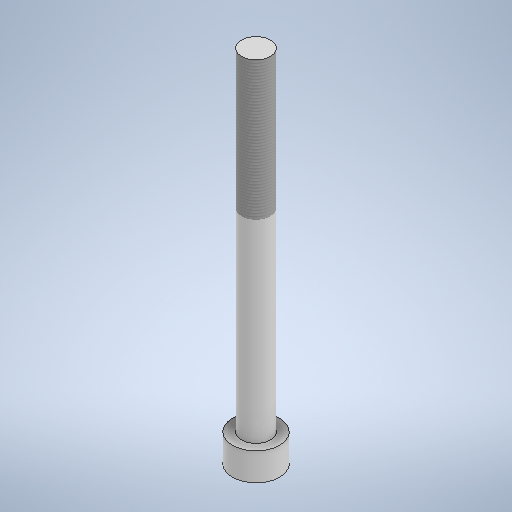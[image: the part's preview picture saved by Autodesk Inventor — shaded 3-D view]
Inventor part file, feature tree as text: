
AUTODESK INVENTOR PART (.ipt)
format: ipt  version: 2025.2 (Build 292293000, 293)  size: 253,952 bytes
history: native  units: mm
features: extrude x2, sketch x2, other x1, thread x1
ambient origin geometry x8: Origin, YZ Plane, XZ Plane, XY Plane, X Axis, Y Axis, Z Axis, Center Point
bodies: Body1 (feature_tree)
feature tree (6):
  other  "Bryła1"
  extrude  "Wyciągnięcie proste1"  Depth=8.5mm
  extrude  "Wyciągnięcie proste2"  Depth=5.0mm TaperAngle=0.0deg
  thread  "Gwint1"
  sketch  "Szkic1"
  sketch  "Szkic2"
